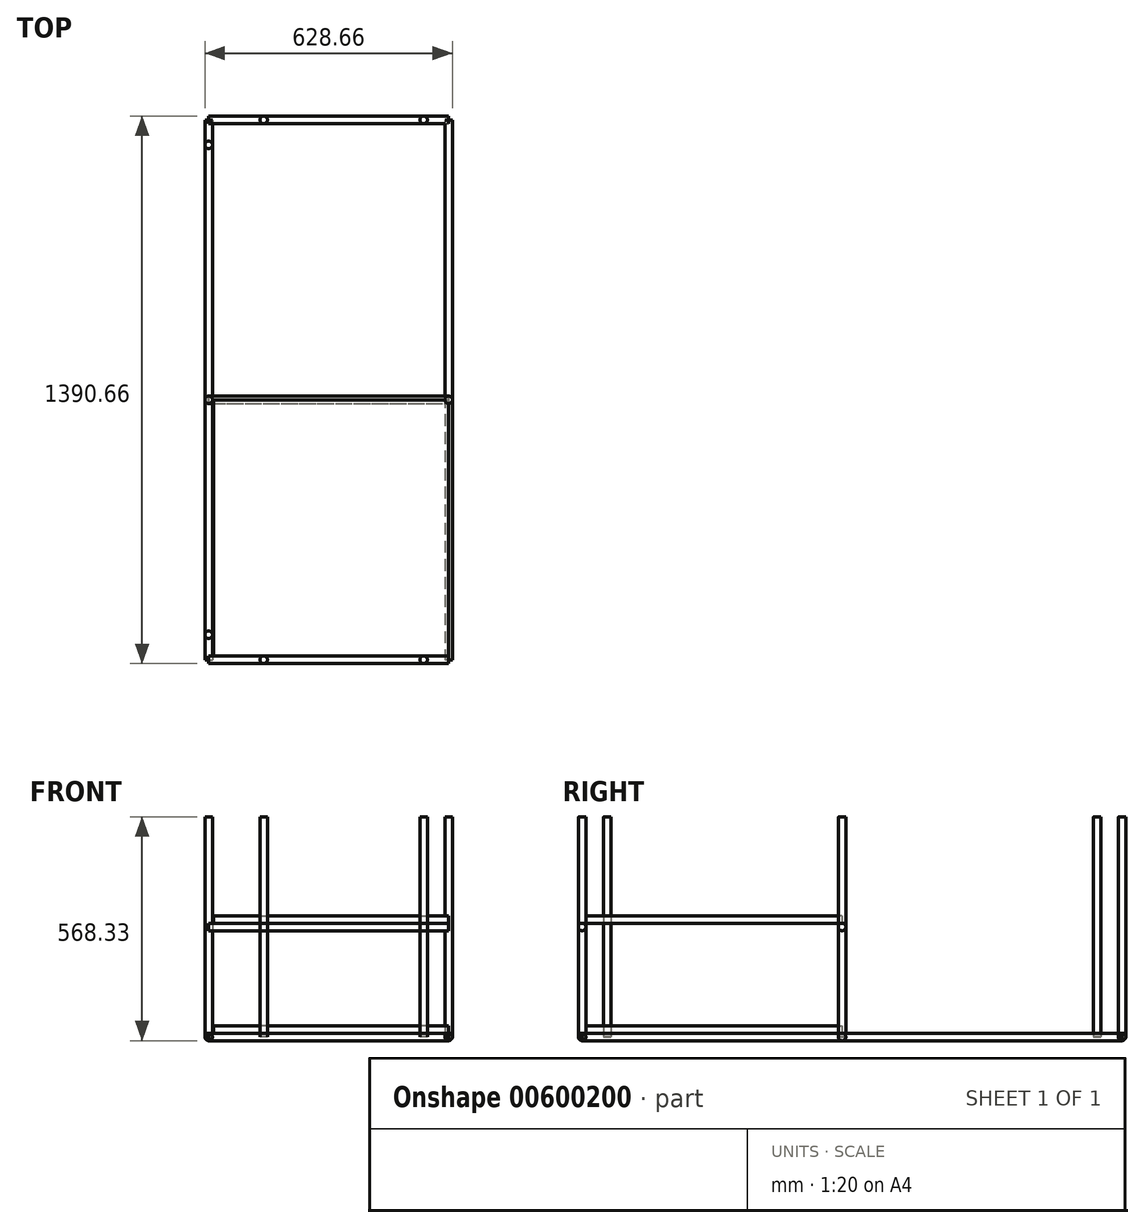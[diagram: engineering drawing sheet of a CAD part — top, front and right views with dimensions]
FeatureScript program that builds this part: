
annotation { "Feature Type Name" : "Feature", "Feature Type Description" : "" }
export const myFeature = defineFeature(function(context is Context, id is Id, definition is map)
    precondition{}
    {
        {
            var Q0;
            Q0=qCreatedBy(makeId("Front.planeOp"),FACE);
            var sketch = newSketch(context, id + "F0", { "sketchPlane" : qUnion([Q0])});
            skCircle(sketch, "E0", {"center": v(0, 0) * mm, "radius": 9.53 * mm});
            skCircle(sketch, "E1", {"center": v(-609.6, 0) * mm, "radius": 9.53 * mm});
            skSolve(sketch);
        }
        {
            var Q0;
            Q0 = qSketchRegion(id + "F0", true);
            extrude(context, id + "F1", {"entities" : qUnion([Q0]), "oppositeDirection" : true, "depth" : 1371.6 * mm, "offsetDistance" : 25.4 * mm});
        }
        {
            var Q0;
            Q0=qCreatedBy(makeId("Right.planeOp"),FACE);
            var sketch = newSketch(context, id + "F2", { "sketchPlane" : qUnion([Q0])});
            skCircle(sketch, "E2", {"center": v(0, 0) * mm, "radius": 9.53 * mm});
            skCircle(sketch, "E3", {"center": v(1371.6, 0) * mm, "radius": 9.53 * mm});
            skSolve(sketch);
        }
        {
            var Q0;
            Q0 = qSketchRegion(id + "F2", true);
            extrude(context, id + "F3", {"entities" : qUnion([Q0]), "oppositeDirection" : true, "depth" : 609.6 * mm, "offsetDistance" : 25.4 * mm});
        }
        {
            var Q0;
            Q0=qCreatedBy(makeId("Top.planeOp"),FACE);
            var sketch = newSketch(context, id + "F4", { "sketchPlane" : qUnion([Q0])});
            skCircle(sketch, "E4", {"center": v(-63.5, 0) * mm, "radius": 9.53 * mm});
            skCircle(sketch, "E5", {"center": v(-469.9, 0) * mm, "radius": 9.52 * mm});
            skCircle(sketch, "E6", {"center": v(-609.6, 63.5) * mm, "radius": 9.52 * mm});
            skCircle(sketch, "E7", {"center": v(-609.6, 1308.1) * mm, "radius": 9.52 * mm});
            skCircle(sketch, "E8", {"center": v(-469.9, 1371.6) * mm, "radius": 9.53 * mm});
            skCircle(sketch, "E9", {"center": v(-63.5, 1371.6) * mm, "radius": 9.52 * mm});
            skCircle(sketch, "E10", {"center": v(-609.6, 660.4) * mm, "radius": 9.52 * mm});
            skCircle(sketch, "E11", {"center": v(0, 660.4) * mm, "radius": 9.52 * mm});
            skSolve(sketch);
        }
        {
            var Q0;
            Q0 = qSketchRegion(id + "F4", true);
            extrude(context, id + "F5", {"entities" : qUnion([Q0]), "depth" : 558.8 * mm, "offsetDistance" : 25.4 * mm});
        }
        {
            var Q0;
            Q0=qCreatedBy(makeId("Right.planeOp"),FACE);
            var sketch = newSketch(context, id + "F6", { "sketchPlane" : qUnion([Q0])});
            skCircle(sketch, "E12", {"center": v(660.4, 0) * mm, "radius": 9.53 * mm});
            skCircle(sketch, "E13", {"center": v(660.4, 279.4) * mm, "radius": 9.53 * mm});
            skCircle(sketch, "E14", {"center": v(0, 279.4) * mm, "radius": 9.52 * mm});
            skSolve(sketch);
        }
        {
            var Q0;
            Q0 = qSketchRegion(id + "F6", true);
            extrude(context, id + "F7", {"entities" : qUnion([Q0]), "oppositeDirection" : true, "depth" : 609.6 * mm, "offsetDistance" : 25.4 * mm});
        }
        {
            var Q0;
            Q0=qCreatedBy(makeId("Top.planeOp"),FACE);
            cPlane(context, id + "F8", {"entities" : qUnion([Q0]), "cplaneType" : CPlaneType.OFFSET, "offset" : 9.52 * mm, "width" : 152.4 * mm, "height" : 152.4 * mm});
        }
        {
            var Q0;
            Q0=qCreatedBy(id+"F8.planeOp",FACE);
            var sketch = newSketch(context, id + "F9", { "sketchPlane" : qUnion([Q0])});
            skLineSegment(sketch, "E15.bottom", {"start": v(0, 9.52) * mm, "end": v(-596.9, 9.52) * mm});
            skLineSegment(sketch, "E15.top", {"start": v(0, 660.4) * mm, "end": v(-596.9, 660.4) * mm});
            skLineSegment(sketch, "E15.left", {"start": v(0, 9.53) * mm, "end": v(0, 660.4) * mm});
            skLineSegment(sketch, "E15.right", {"start": v(-596.9, 9.52) * mm, "end": v(-596.9, 660.4) * mm});
            skSolve(sketch);
        }
        {
            var Q0;
            Q0 = qSketchRegion(id + "F9", true);
            extrude(context, id + "F10", {"entities" : qUnion([Q0]), "depth" : 19.05 * mm, "offsetDistance" : 25.4 * mm});
        }
        {
            var Q0;
            Q0=qCreatedBy(makeId("Top.planeOp"),FACE);
            cPlane(context, id + "F11", {"entities" : qUnion([Q0]), "cplaneType" : CPlaneType.OFFSET, "offset" : 288.93 * mm, "width" : 152.4 * mm, "height" : 152.4 * mm});
        }
        {
            var Q0;
            Q0=qCreatedBy(id+"F11.planeOp",FACE);
            var sketch = newSketch(context, id + "F12", { "sketchPlane" : qUnion([Q0])});
            skLineSegment(sketch, "E16.bottom", {"start": v(-596.9, 660.4) * mm, "end": v(0, 660.4) * mm});
            skLineSegment(sketch, "E16.top", {"start": v(-596.9, 9.52) * mm, "end": v(0, 9.53) * mm});
            skLineSegment(sketch, "E16.left", {"start": v(-596.9, 660.4) * mm, "end": v(-596.9, 9.52) * mm});
            skLineSegment(sketch, "E16.right", {"start": v(0, 660.4) * mm, "end": v(0, 9.53) * mm});
            skSolve(sketch);
        }
        {
            var Q0;
            Q0 = qSketchRegion(id + "F12", true);
            extrude(context, id + "F13", {"entities" : qUnion([Q0]), "depth" : 19.05 * mm, "offsetDistance" : 25.4 * mm});
        }
    });
